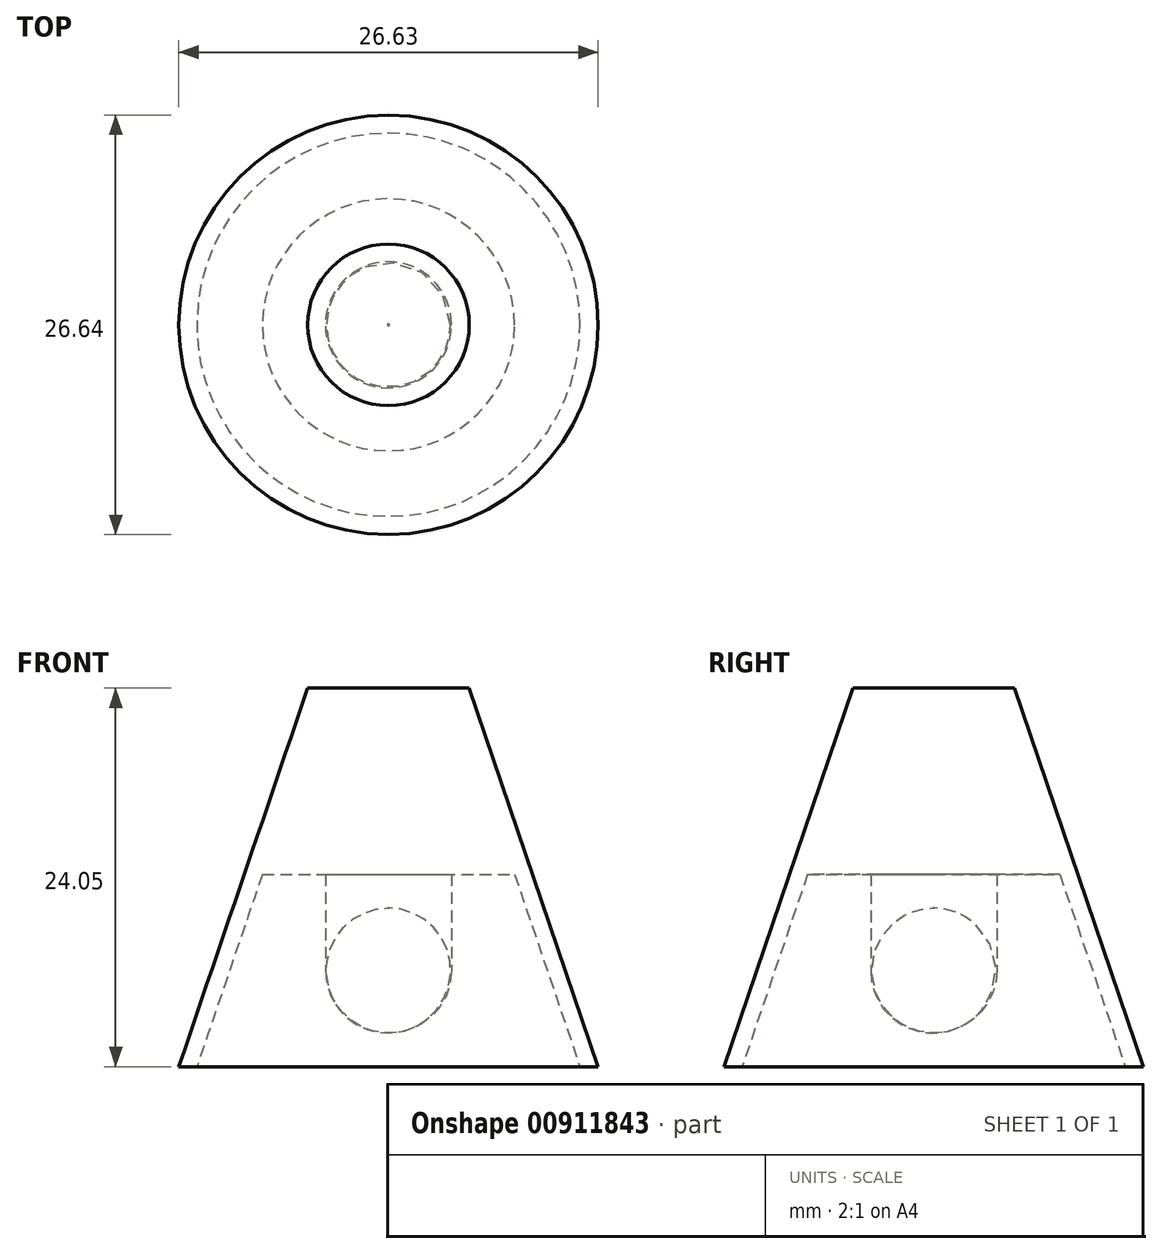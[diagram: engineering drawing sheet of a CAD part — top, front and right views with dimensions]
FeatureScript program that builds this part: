
annotation { "Feature Type Name" : "Feature", "Feature Type Description" : "" }
export const myFeature = defineFeature(function(context is Context, id is Id, definition is map)
    precondition{}
    {
        {
            var Q0;
            Q0=qCreatedBy(makeId("Front.planeOp"),FACE);
            var sketch = newSketch(context, id + "F0", { "sketchPlane" : qUnion([Q0])});
            skLineSegment(sketch, "E0", {"start": v(-45.77, -40.69) * mm, "end": v(-37.58, -16.64) * mm});
            skLineSegment(sketch, "E1", {"start": v(-37.58, -16.64) * mm, "end": v(-32.45, -16.64) * mm});
            skLineSegment(sketch, "E2", {"start": v(-32.45, -16.64) * mm, "end": v(-32.45, -27.64) * mm});
            skLineSegment(sketch, "E3", {"start": v(-32.45, -27.64) * mm, "end": v(-41.33, -27.64) * mm});
            skLineSegment(sketch, "E4", {"start": v(-32.45, -44.78) * mm, "end": v(-32.45, -5.39) * mm});
            skLineSegment(sketch, "E5", {"start": v(-45.77, -40.69) * mm, "end": v(-44.62, -40.69) * mm});
            skLineSegment(sketch, "E6", {"start": v(-44.62, -40.69) * mm, "end": v(-40.46, -28.47) * mm});
            skLineSegment(sketch, "E7", {"start": v(-40.46, -28.47) * mm, "end": v(-32.45, -28.47) * mm});
            skLineSegment(sketch, "E8", {"start": v(-36.46, -28.47) * mm, "end": v(-36.46, -34.58) * mm});
            skPoint(sketch, "E8.endSnap0", {"position": v(-42.54, -34.58) * mm});
            skArc(sketch, "E9", {"start": v(-36.46, -34.58) * mm, "mid": v(-35.28, -37.4) * mm, "end": v(-32.45, -38.55) * mm});
            skSolve(sketch);
        }
        {
            var Q0;
            {var subQ0=sQuery(id+"F0.wireOp",EDGE,"E1");Q0=makeQuery(id+"F0.imprint","IMPRINT",FACE,{"disambiguationData":[TD([[makeQuery(id+"F0.imprint","IMPRINT",EDGE,{"derivedFrom":subQ0}),-1.0]])]});}
            var Q1;
            {var subQ2=sQuery(id+"F0.wireOp",EDGE,"E3");Q1=makeQuery(id+"F0.imprint","IMPRINT",FACE,{"disambiguationData":[TD([[makeQuery(id+"F0.imprint","IMPRINT",EDGE,{"derivedFrom":subQ2}),1.0]])]});}
            var Q2;
            {var subQ4=sQuery(id+"F0.wireOp",EDGE,"E8");Q2=makeQuery(id+"F0.imprint","IMPRINT",FACE,{"disambiguationData":[TD([[makeQuery(id+"F0.imprint","IMPRINT",EDGE,{"derivedFrom":subQ4}),1.0]])]});}
            var Q3;
            Q3=sQuery(id+"F0.wireOp",EDGE,"E4");
            revolve(context, id + "F1", {"surfaceOperationType" : NewSurfaceOperationType.NEW, "entities" : qUnion([Q0, Q1, Q2]), "axis" : qUnion([Q3]), "revolveType" : RevolveType.FULL});
        }
    });
